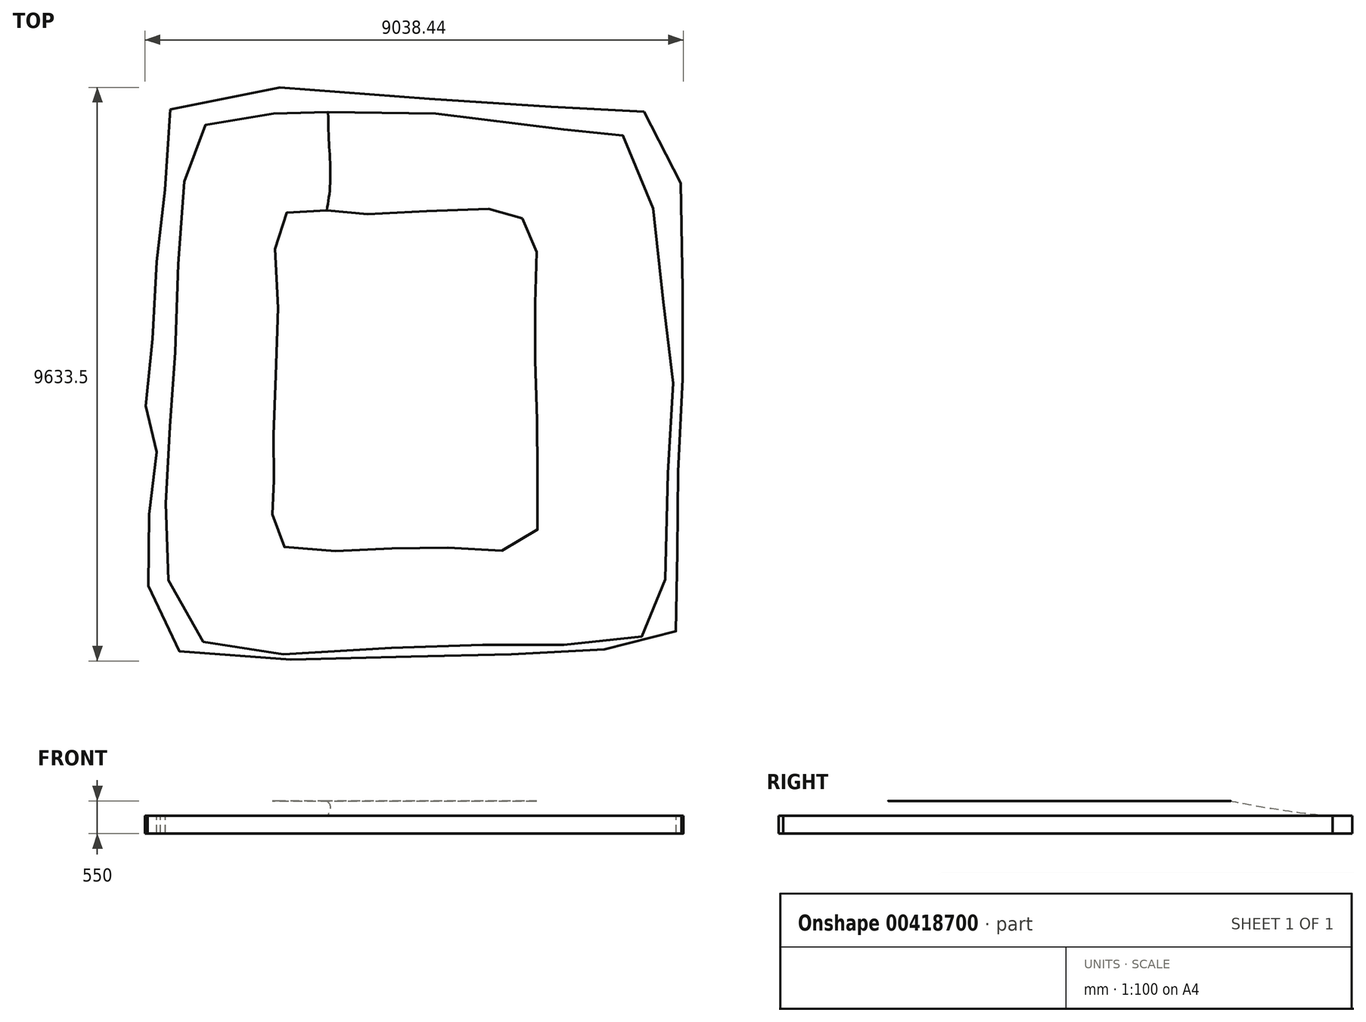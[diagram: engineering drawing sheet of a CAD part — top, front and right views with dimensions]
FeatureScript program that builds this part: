
annotation { "Feature Type Name" : "Feature", "Feature Type Description" : "" }
export const myFeature = defineFeature(function(context is Context, id is Id, definition is map)
    precondition{}
    {
        {
            var Q0;
            Q0=qCreatedBy(makeId("Top.planeOp"),FACE);
            var sketch = newSketch(context, id + "F0", { "sketchPlane" : qUnion([Q0])});
            skFitSpline(sketch, "E0", {"points": [v(-3931.52, 4604.73) * mm, v(-4019.76, 3192.92) * mm, v(-4160.94, 2063.47) * mm, v(-4231.53, 757.54) * mm, v(-4355.07, -266.02) * mm, v(-4231.53, -830.75) * mm, v(-4160.94, -1254.29) * mm, v(-4284.48, -2171.97) * mm, v(-4302.13, -3266.12) * mm, v(-3949.17, -4395.57) * mm, v(-1266.73, -4607.34) * mm, v(1345.13, -4572.05) * mm, v(3251.07, -4466.16) * mm, v(4521.7, -4219.1) * mm, v(4592.3, -2913.17) * mm, v(4592.3, -1501.36) * mm, v(4680.53, 369.3) * mm, v(4662.89, 2222.3) * mm, v(4345.23, 4357.67) * mm, v(2915.77, 4640.03) * mm, v(-419.64, 4851.8) * mm, v(-3931.52, 4604.73) * mm]});
            skSolve(sketch);
        }
        {
            var Q0;
            Q0 = qSketchRegion(id + "F0", true);
            extrude(context, id + "F1", {"entities" : qUnion([Q0]), "oppositeDirection" : true, "depth" : 300 * mm, "offsetDistance" : 25 * mm});
        }
        {
            var Q0;
            Q0=qCreatedBy(makeId("Top.planeOp"),FACE);
            cPlane(context, id + "F2", {"entities" : qUnion([Q0]), "cplaneType" : CPlaneType.OFFSET, "offset" : 50 * mm, "width" : 150 * mm, "height" : 150 * mm});
        }
        {
            var Q0;
            Q0=qCreatedBy(makeId("Top.planeOp"),FACE);
            cPlane(context, id + "F3", {"entities" : qUnion([Q0]), "cplaneType" : CPlaneType.OFFSET, "offset" : 100 * mm, "width" : 150 * mm, "height" : 150 * mm});
        }
        {
            var Q0;
            Q0=qCreatedBy(makeId("Top.planeOp"),FACE);
            cPlane(context, id + "F4", {"entities" : qUnion([Q0]), "cplaneType" : CPlaneType.OFFSET, "offset" : 150 * mm, "width" : 150 * mm, "height" : 150 * mm});
        }
        {
            var Q0;
            Q0=qCreatedBy(makeId("Top.planeOp"),FACE);
            cPlane(context, id + "F5", {"entities" : qUnion([Q0]), "cplaneType" : CPlaneType.OFFSET, "offset" : 200 * mm, "width" : 150 * mm, "height" : 150 * mm});
        }
        {
            var Q0;
            Q0=qCreatedBy(makeId("Top.planeOp"),FACE);
            cPlane(context, id + "F6", {"entities" : qUnion([Q0]), "cplaneType" : CPlaneType.OFFSET, "offset" : 250 * mm, "width" : 150 * mm, "height" : 150 * mm});
        }
        {
            var Q0;
            Q0=qCreatedBy(id+"F6.planeOp",FACE);
            var sketch = newSketch(context, id + "F7", { "sketchPlane" : qUnion([Q0])});
            skFitSpline(sketch, "E1", {"points": [v(-1305.41, 2908.24) * mm, v(-1870.27, 2908.24) * mm, v(-2127.03, 2690) * mm, v(-2152.7, 1932.58) * mm, v(-2127.03, 648.8) * mm, v(-2204.05, -699.15) * mm, v(-2178.38, -1353.87) * mm, v(-2216.89, -1995.75) * mm, v(-2216.89, -2201.16) * mm, v(-2165.54, -2637.64) * mm, v(-1549.33, -2817.36) * mm, v(-586.5, -2791.69) * mm, v(466.19, -2753.18) * mm, v(1377.66, -2791.69) * mm, v(2135.09, -2688.99) * mm, v(2237.79, -1816.03) * mm, v(2237.79, -917.39) * mm, v(2199.27, 186.65) * mm, v(2199.27, 1239.34) * mm, v(2212.11, 2137.98) * mm, v(2186.44, 2600.14) * mm, v(1672.93, 2908.24) * mm, v(1416.18, 2933.92) * mm, v(132.4, 2882.57) * mm, v(-791.9, 2844.05) * mm, v(-1305.41, 2908.24) * mm]});
            skSolve(sketch);
        }
        {
            var Q0;
            Q0=qCreatedBy(id+"F5.planeOp",FACE);
            var sketch = newSketch(context, id + "F8", { "sketchPlane" : qUnion([Q0])});
            skFitSpline(sketch, "E2", {"points": [v(-1872.12, 3279.81) * mm, v(-2382.28, 3088.5) * mm, v(-2509.83, 2562.4) * mm, v(-2541.71, 1813.1) * mm, v(-2509.83, 952.2) * mm, v(-2573.6, -227.55) * mm, v(-2573.6, -833.37) * mm, v(-2605.48, -1534.84) * mm, v(-2637.37, -2204.43) * mm, v(-2621.42, -2682.7) * mm, v(-2031.55, -3129.1) * mm, v(-915.57, -3176.93) * mm, v(312.01, -3192.87) * mm, v(1443.93, -3129.1) * mm, v(2416.43, -3033.44) * mm, v(2719.34, -2427.63) * mm, v(2719.34, -1247.88) * mm, v(2591.8, -323.2) * mm, v(2591.8, 410.15) * mm, v(2591.8, 1781.21) * mm, v(2559.91, 1988.47) * mm, v(2607.74, 2689.94) * mm, v(1316.4, 3263.87) * mm, v(-261.92, 3200.1) * mm, v(-1170.65, 3184.16) * mm, v(-1872.12, 3279.81) * mm]});
            skSolve(sketch);
        }
        {
            var Q0;
            Q0=qCreatedBy(id+"F4.planeOp",FACE);
            var sketch = newSketch(context, id + "F9", { "sketchPlane" : qUnion([Q0])});
            skFitSpline(sketch, "E3", {"points": [v(-1305.85, 3463.4) * mm, v(-1784.13, 3495.28) * mm, v(-2389.95, 3399.63) * mm, v(-2692.86, 3080.78) * mm, v(-2708.8, 2331.47) * mm, v(-2772.57, 1693.77) * mm, v(-2772.57, 848.82) * mm, v(-2963.88, -235.28) * mm, v(-2963.88, -809.21) * mm, v(-2995.77, -1478.8) * mm, v(-2963.88, -2244.04) * mm, v(-2947.94, -2897.7) * mm, v(-2326.18, -3391.9) * mm, v(-1114.54, -3487.57) * mm, v(304.35, -3455.68) * mm, v(2233.4, -3471.62) * mm, v(2918.93, -2977.4) * mm, v(3221.84, -2275.93) * mm, v(3062.41, -968.64) * mm, v(2918.93, 274.88) * mm, v(2902.99, 1231.44) * mm, v(2966.76, 2283.65) * mm, v(2934.87, 2969.18) * mm, v(1755.12, 3463.4) * mm, v(-827.58, 3463.4) * mm, v(-1305.85, 3463.4) * mm]});
            skSolve(sketch);
        }
        {
            var Q0;
            Q0=qCreatedBy(id+"F3.planeOp",FACE);
            var sketch = newSketch(context, id + "F10", { "sketchPlane" : qUnion([Q0])});
            skFitSpline(sketch, "E4", {"points": [v(-1808.35, 3774.03) * mm, v(-2509.83, 3694.32) * mm, v(-2892.45, 3391.41) * mm, v(-3019.99, 2865.3) * mm, v(-2956.22, 2116) * mm, v(-3083.76, 1302.94) * mm, v(-3243.18, 0) * mm, v(-3179.41, -1152.22) * mm, v(-3275.07, -2045) * mm, v(-3275.07, -2714.6) * mm, v(-3051.87, -3495.78) * mm, v(-1983.72, -4005.94) * mm, v(-660.49, -3878.4) * mm, v(614.92, -3894.34) * mm, v(2464.26, -3862.46) * mm, v(3229.5, -3352.3) * mm, v(3548.35, -2300.09) * mm, v(3675.9, -833.37) * mm, v(3293.27, 729) * mm, v(3229.5, 1876.87) * mm, v(3229.5, 2833.42) * mm, v(2799.05, 3598.67) * mm, v(1699.01, 3774.03) * mm, v(1443.93, 3774.03) * mm, v(-453.23, 3789.98) * mm, v(-1808.35, 3774.03) * mm]});
            skSolve(sketch);
        }
        {
            var Q0;
            Q0=qCreatedBy(id+"F2.planeOp",FACE);
            var sketch = newSketch(context, id + "F11", { "sketchPlane" : qUnion([Q0])});
            skFitSpline(sketch, "E5", {"points": [v(-1106.88, 4140.71) * mm, v(-1776.47, 4092.89) * mm, v(-2701.14, 4029.12) * mm, v(-3259.13, 3694.32) * mm, v(-3338.84, 2865.3) * mm, v(-3386.67, 1908.75) * mm, v(-3514.2, 1207.28) * mm, v(-3577.98, 521.75) * mm, v(-3593.92, -355.1) * mm, v(-3562.04, -1152.22) * mm, v(-3721.46, -2013.12) * mm, v(-3721.46, -2746.48) * mm, v(-3514.2, -3304.47) * mm, v(-3386.67, -3814.63) * mm, v(-2764.9, -4085.65) * mm, v(-1553.27, -4245.08) * mm, v(-341.64, -4276.97) * mm, v(678.69, -4213.2) * mm, v(2591.8, -4117.54) * mm, v(3739.66, -3990) * mm, v(4058.52, -3065.33) * mm, v(4090.4, -1726.15) * mm, v(4058.52, -259.44) * mm, v(3739.66, 1366.7) * mm, v(3675.9, 2195.72) * mm, v(3484.58, 3534.9) * mm, v(2783.1, 3981.29) * mm, v(232.3, 4076.94) * mm, v(-1106.88, 4140.71) * mm]});
            skSolve(sketch);
        }
        {
            var Q0;
            Q0=qCreatedBy(makeId("Top.planeOp"),FACE);
            var sketch = newSketch(context, id + "F12", { "sketchPlane" : qUnion([Q0])});
            skFitSpline(sketch, "E6", {"points": [v(-2956.22, 4459.57) * mm, v(-3402.6, 4284.2) * mm, v(-3657.7, 3598.67) * mm, v(-3785.23, 2387.03) * mm, v(-3833.06, 792.77) * mm, v(-3912.77, -307.26) * mm, v(-3976.54, -1518.9) * mm, v(-4024.37, -2587.05) * mm, v(-3833.06, -3766.8) * mm, v(-3195.36, -4436.4) * mm, v(-1680.81, -4532.05) * mm, v(551.15, -4404.5) * mm, v(1826.55, -4388.56) * mm, v(3229.5, -4372.62) * mm, v(4154.17, -4149.43) * mm, v(4377.37, -3368.24) * mm, v(4441.14, -1184.1) * mm, v(4504.9, 250.73) * mm, v(4313.6, 1621.79) * mm, v(4090.4, 3343.59) * mm, v(3612.12, 4204.48) * mm, v(3245.44, 4220.43) * mm, v(614.92, 4523.34) * mm, v(-1425.73, 4555.22) * mm, v(-1712.7, 4555.22) * mm, v(-2956.22, 4459.57) * mm]});
            skSolve(sketch);
        }
        {
            var Q1;
            Q1=makeQuery(id+"F7.imprint","IMPRINT",FACE,{"disambiguationData":[TD([[makeQuery(id+"F7.imprint","IMPRINT",EDGE,{"derivedFrom":sQuery(id+"F7.wireOp",EDGE,"E1")}),1.0]])]});
            var Q2;
            Q2=makeQuery(id+"F8.imprint","IMPRINT",FACE,{"disambiguationData":[TD([[makeQuery(id+"F8.imprint","IMPRINT",EDGE,{"derivedFrom":sQuery(id+"F8.wireOp",EDGE,"E2")}),1.0]])]});
            var Q3;
            Q3=makeQuery(id+"F9.imprint","IMPRINT",FACE,{"disambiguationData":[TD([[makeQuery(id+"F9.imprint","IMPRINT",EDGE,{"derivedFrom":sQuery(id+"F9.wireOp",EDGE,"E3")}),1.0]])]});
            var Q4;
            Q4=makeQuery(id+"F10.imprint","IMPRINT",FACE,{"disambiguationData":[TD([[makeQuery(id+"F10.imprint","IMPRINT",EDGE,{"derivedFrom":sQuery(id+"F10.wireOp",EDGE,"E4")}),1.0]])]});
            var Q5;
            Q5=makeQuery(id+"F11.imprint","IMPRINT",FACE,{"disambiguationData":[TD([[makeQuery(id+"F11.imprint","IMPRINT",EDGE,{"derivedFrom":sQuery(id+"F11.wireOp",EDGE,"E5")}),1.0]])]});
            var Q6;
            Q6=makeQuery(id+"F12.imprint","IMPRINT",FACE,{"disambiguationData":[TD([[makeQuery(id+"F12.imprint","IMPRINT",EDGE,{"derivedFrom":sQuery(id+"F12.wireOp",EDGE,"E6")}),1.0]])]});
            loft(context, id + "F13", {"operationType" : NewBodyOperationType.ADD, "sheetProfilesArray" : [{ "sheetProfileEntities" : qUnion([Q1]) }, { "sheetProfileEntities" : qUnion([Q2]) }, { "sheetProfileEntities" : qUnion([Q3]) }, { "sheetProfileEntities" : qUnion([Q4]) }, { "sheetProfileEntities" : qUnion([Q5]) }, { "sheetProfileEntities" : qUnion([Q6]) }]});
        }
    });
